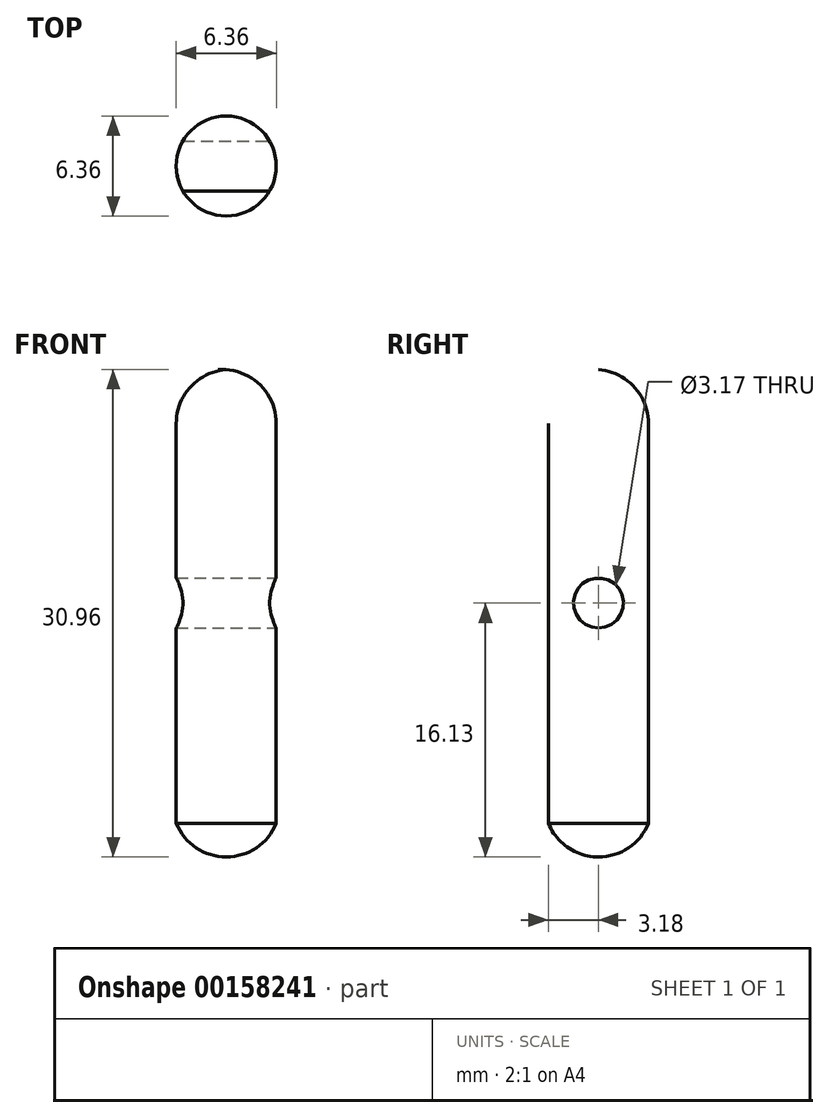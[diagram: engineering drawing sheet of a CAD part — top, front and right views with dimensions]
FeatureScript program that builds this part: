
annotation { "Feature Type Name" : "Feature", "Feature Type Description" : "" }
export const myFeature = defineFeature(function(context is Context, id is Id, definition is map)
    precondition{}
    {
        {
            var Q0;
            Q0=qCreatedBy(makeId("Right.planeOp"),FACE);
            var sketch = newSketch(context, id + "F0", { "sketchPlane" : qUnion([Q0])});
            skLineSegment(sketch, "E0.left", {"start": v(-3.18, 11.4) * mm, "end": v(-3.17, -14) * mm});
            skPoint(sketch, "E0.middle", {"position": v(0, 0) * mm});
            skArc(sketch, "E1", {"start": v(-3.17, -14) * mm, "mid": v(-1.91, -15.55) * mm, "end": v(0, -16.13) * mm});
            skLineSegment(sketch, "E2", {"start": v(0, -16.93) * mm, "end": v(0, 15.66) * mm});
            skArc(sketch, "E3", {"start": v(0, 14.82) * mm, "mid": v(-2.26, 13.74) * mm, "end": v(-3.18, 11.4) * mm});
            skLineSegment(sketch, "E4", {"start": v(0, 0) * mm, "end": v(10.4, 0) * mm});
            skSolve(sketch);
        }
        {
            var Q0;
            Q0 = qSketchRegion(id + "F0", true);
            var Q1;
            Q1=sQuery(id+"F0.wireOp",EDGE,"E2");
            revolve(context, id + "F1", {"entities" : qUnion([Q0]), "axis" : qUnion([Q1]), "revolveType" : RevolveType.FULL});
        }
        {
            var Q0;
            Q0=qCreatedBy(makeId("Right.planeOp"),FACE);
            var sketch = newSketch(context, id + "F2", { "sketchPlane" : qUnion([Q0])});
            skCircle(sketch, "E5", {"center": v(0, 0) * mm, "radius": 1.59 * mm});
            skSolve(sketch);
        }
        {
            var Q0;
            Q0 = qSketchRegion(id + "F2", true);
            extrude(context, id + "F3", {"entities" : qUnion([Q0]), "operationType" : NewBodyOperationType.REMOVE, "endBound" : BoundingType.THROUGH_ALL, "oppositeDirection" : true, "depth" : 25.4 * mm, "hasSecondDirection" : true, "secondDirectionOppositeDirection" : false, "secondDirectionDepth" : 25.4 * mm});
        }
    });
